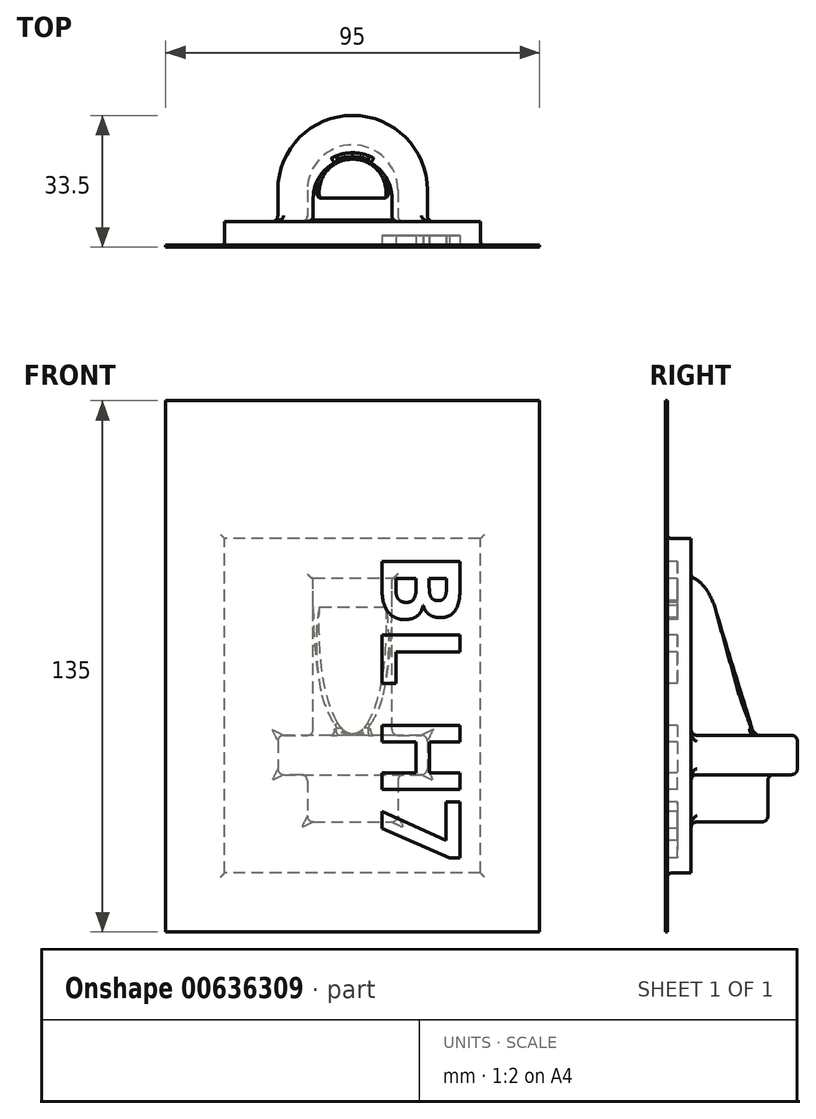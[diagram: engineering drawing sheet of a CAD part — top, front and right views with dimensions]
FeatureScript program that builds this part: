
annotation { "Feature Type Name" : "Feature", "Feature Type Description" : "" }
export const myFeature = defineFeature(function(context is Context, id is Id, definition is map)
    precondition{}
    {
        {
            var Q0;
            Q0=qCreatedBy(makeId("Right.planeOp"),FACE);
            var sketch = newSketch(context, id + "F0", { "sketchPlane" : qUnion([Q0])});
            skLineSegment(sketch, "E0", {"start": v(0, 0) * mm, "end": v(0, 135) * mm});
            skLineSegment(sketch, "E1", {"start": v(0, 135) * mm, "end": v(0.5, 135) * mm});
            skLineSegment(sketch, "E2", {"start": v(0.5, 135) * mm, "end": v(0.5, 100) * mm});
            skLineSegment(sketch, "E3", {"start": v(0.5, 100) * mm, "end": v(35.5, 100) * mm});
            skLineSegment(sketch, "E4", {"start": v(35.5, 100) * mm, "end": v(35.5, 15) * mm});
            skLineSegment(sketch, "E5", {"start": v(35.5, 15) * mm, "end": v(0.5, 15) * mm});
            skLineSegment(sketch, "E6", {"start": v(0.5, 15) * mm, "end": v(0.5, 0) * mm});
            skLineSegment(sketch, "E7", {"start": v(0.5, 0) * mm, "end": v(0, 0) * mm});
            skSolve(sketch);
        }
        {
            var Q0;
            Q0=qSketchRegion(id+"F0",true);
            extrude(context, id + "F1", {"entities" : qUnion([Q0]), "depth" : 95 * mm, "offsetDistance" : 25 * mm});
        }
        {
            var Q0;
            Q0=makeQuery(id+"F1.opExtrude","SWEPT_FACE",FACE,{"disambiguationData":[OSD([sQuery(id+"F0.wireOp",EDGE,"E4")])]});
            var sketch = newSketch(context, id + "F2", { "sketchPlane" : qUnion([Q0])});
            skLineSegment(sketch, "E8.bottom", {"start": v(-95, 100) * mm, "end": v(-80, 100) * mm});
            skLineSegment(sketch, "E8.top", {"start": v(-95, 15) * mm, "end": v(-80, 15) * mm});
            skLineSegment(sketch, "E8.left", {"start": v(-95, 100) * mm, "end": v(-95, 15) * mm});
            skLineSegment(sketch, "E8.right", {"start": v(-80, 100) * mm, "end": v(-80, 15) * mm});
            skLineSegment(sketch, "E9.bottom", {"start": v(0, 100) * mm, "end": v(-15, 100) * mm});
            skLineSegment(sketch, "E9.top", {"start": v(0, 15) * mm, "end": v(-15, 15) * mm});
            skLineSegment(sketch, "E9.left", {"start": v(0, 100) * mm, "end": v(0, 15) * mm});
            skLineSegment(sketch, "E9.right", {"start": v(-15, 100) * mm, "end": v(-15, 15) * mm});
            skSolve(sketch);
        }
        {
            var Q0;
            Q0=qSketchRegion(id+"F2",true);
            var Q1;
            Q1=makeQuery(id+"F1.opExtrude","SWEPT_FACE",FACE,{"disambiguationData":[OSD([sQuery(id+"F0.wireOp",EDGE,"E2")])]});
            extrude(context, id + "F3", {"entities" : qUnion([Q0]), "operationType" : NewBodyOperationType.REMOVE, "endBound" : BoundingType.UP_TO_SURFACE, "oppositeDirection" : true, "depth" : 25 * mm, "endBoundEntityFace" : qUnion([Q1]), "offsetDistance" : 25 * mm});
        }
        {
            var Q0;
            Q0=makeQuery(id+"F1.opExtrude","SWEPT_FACE",FACE,{"disambiguationData":[OSD([sQuery(id+"F0.wireOp",EDGE,"E0")])]});
            var sketch = newSketch(context, id + "F4", { "sketchPlane" : qUnion([Q0])});
            skText(sketch, "E10", { "text": "BL H7", "fontName": "OpenSans-Bold.ttf"});
            const initialGuessF4  = {"E10": [0.055, 0.0966, 0, -1, 0.02]};
            skSetInitialGuess(sketch, initialGuessF4);
            skSolve(sketch);
        }
        {
            var Q0;
            Q0 = qSketchRegion(id + "F4", true);
            extrude(context, id + "F5", {"entities" : qUnion([Q0]), "operationType" : NewBodyOperationType.REMOVE, "oppositeDirection" : true, "depth" : 3 * mm, "offsetDistance" : 25 * mm});
        }
        {
            var Q0;
            Q0=makeQuery(id+"F1.opExtrude","SWEPT_FACE",FACE,{"disambiguationData":[OSD([sQuery(id+"F0.wireOp",EDGE,"E5")])]});
            var sketch = newSketch(context, id + "F6", { "sketchPlane" : qUnion([Q0])});
            skLineSegment(sketch, "E11", {"start": v(80, -6.5) * mm, "end": v(66.5, -6.5) * mm});
            skLineSegment(sketch, "E12", {"start": v(47.5, -3.09) * mm, "end": v(47.5, -30.76) * mm, "construction": true});
            skPoint(sketch, "E12.startSnap0", {"position": v(47.5, -6.5) * mm});
            skLineSegment(sketch, "E13", {"start": v(66.5, -6.5) * mm, "end": v(66.5, -14.5) * mm});
            skLineSegment(sketch, "E14", {"start": v(28.5, -6.5) * mm, "end": v(28.5, -14.5) * mm});
            skArc(sketch, "E15", {"start": v(66.5, -14.5) * mm, "mid": v(47.5, -33.5) * mm, "end": v(28.5, -14.5) * mm});
            skLineSegment(sketch, "E16", {"start": v(80, -6.5) * mm, "end": v(83.42, -6.5) * mm});
            skLineSegment(sketch, "E17", {"start": v(83.42, -6.5) * mm, "end": v(83.42, -40.14) * mm});
            skLineSegment(sketch, "E18", {"start": v(83.42, -40.14) * mm, "end": v(10.55, -40.14) * mm});
            skLineSegment(sketch, "E19", {"start": v(10.55, -40.14) * mm, "end": v(10.55, -6.5) * mm});
            skLineSegment(sketch, "E20", {"start": v(10.55, -6.5) * mm, "end": v(15, -6.5) * mm});
            skLineSegment(sketch, "E21.trimOffspring", {"start": v(28.5, -6.5) * mm, "end": v(15, -6.5) * mm});
            skLineSegment(sketch, "E22.0", {"start": v(36, -6.5) * mm, "end": v(36, -14.5) * mm});
            skArc(sketch, "E22.1", {"start": v(59, -14.5) * mm, "mid": v(47.5, -26) * mm, "end": v(36, -14.5) * mm});
            skLineSegment(sketch, "E22.2", {"start": v(59, -6.5) * mm, "end": v(59, -14.5) * mm});
            skLineSegment(sketch, "E23", {"start": v(66.5, -6.5) * mm, "end": v(59, -6.5) * mm});
            skLineSegment(sketch, "E24", {"start": v(36, -6.5) * mm, "end": v(28.5, -6.5) * mm});
            skSolve(sketch);
        }
        {
            var Q0;
            {var subQ4=sQuery(id+"F6.wireOp",EDGE,"E16");Q0=makeQuery(id+"F6.imprint","IMPRINT",FACE,{"disambiguationData":[TD([[makeQuery(id+"F6.imprint","IMPRINT",EDGE,{"derivedFrom":subQ4}),-1.0]])]});}
            var Q1;
            {var subQ0=sQuery(id+"F6.wireOp",EDGE,"E11");Q1=makeQuery(id+"F6.imprint","IMPRINT",FACE,{"disambiguationData":[TD([[makeQuery(id+"F6.imprint","IMPRINT",EDGE,{"derivedFrom":subQ0}),1.0]])]});}
            var Q2;
            Q2=makeQuery(id+"F1.opExtrude","SWEPT_FACE",FACE,{"disambiguationData":[OSD([sQuery(id+"F0.wireOp",EDGE,"E3")])]});
            extrude(context, id + "F7", {"entities" : qUnion([Q0, Q1]), "operationType" : NewBodyOperationType.REMOVE, "endBound" : BoundingType.UP_TO_SURFACE, "oppositeDirection" : true, "depth" : 20 * mm, "endBoundEntityFace" : qUnion([Q2]), "offsetDistance" : 25 * mm});
        }
        {
            var Q0;
            Q0 = qSketchRegion(id + "F6", true);
            extrude(context, id + "F8", {"entities" : qUnion([Q0]), "operationType" : NewBodyOperationType.REMOVE, "oppositeDirection" : true, "depth" : 25 * mm, "offsetDistance" : 25 * mm});
        }
        {
            var Q0;
            Q0=makeQuery(id+"F1.opExtrude","SWEPT_FACE",FACE,{"disambiguationData":[OSD([sQuery(id+"F0.wireOp",EDGE,"E3")])]});
            var sketch = newSketch(context, id + "F9", { "sketchPlane" : qUnion([Q0])});
            skLineSegment(sketch, "E25", {"start": v(28.5, 6.5) * mm, "end": v(37.5, 6.5) * mm});
            skPoint(sketch, "E26", {"position": v(47.5, 6.5) * mm});
            skLineSegment(sketch, "E27", {"start": v(37.5, 6.5) * mm, "end": v(37.5, 12.5) * mm});
            skLineSegment(sketch, "E28", {"start": v(57.5, 6.5) * mm, "end": v(57.5, 12.5) * mm});
            skLineSegment(sketch, "E29", {"start": v(47.5, 3.35) * mm, "end": v(47.5, 29.33) * mm, "construction": true});
            skArc(sketch, "E30", {"start": v(37.5, 12.5) * mm, "mid": v(47.5, 22.5) * mm, "end": v(57.5, 12.5) * mm});
            skLineSegment(sketch, "E31", {"start": v(28.5, 6.5) * mm, "end": v(24.68, 6.5) * mm});
            skLineSegment(sketch, "E32", {"start": v(24.68, 6.5) * mm, "end": v(24.68, 41.76) * mm});
            skLineSegment(sketch, "E33", {"start": v(24.68, 41.76) * mm, "end": v(72, 41.76) * mm});
            skLineSegment(sketch, "E34", {"start": v(72, 41.76) * mm, "end": v(72, 6.5) * mm});
            skLineSegment(sketch, "E35", {"start": v(72, 6.5) * mm, "end": v(66.5, 6.5) * mm});
            skLineSegment(sketch, "E36.trimOffspring", {"start": v(57.5, 6.5) * mm, "end": v(66.5, 6.5) * mm});
            skSolve(sketch);
        }
        {
            var Q0;
            Q0 = qSketchRegion(id + "F9", true);
            extrude(context, id + "F10", {"entities" : qUnion([Q0]), "operationType" : NewBodyOperationType.REMOVE, "oppositeDirection" : true, "depth" : 50 * mm, "offsetDistance" : 25 * mm});
        }
        {
            var Q0;
            Q0=makeQuery(id+"F3.boolean.opBoolean","COPY",FACE,{"derivedFrom":makeQuery(id+"F3.opExtrude","SWEPT_FACE",FACE,{"disambiguationData":[OSD([sQuery(id+"F2.wireOp",EDGE,"E8.right")])]})});
            var sketch = newSketch(context, id + "F11", { "sketchPlane" : qUnion([Q0])});
            skLineSegment(sketch, "E37", {"start": v(6.5, 106.69) * mm, "end": v(6.5, 100) * mm});
            skLineSegment(sketch, "E38", {"start": v(6.5, 100) * mm, "end": v(6.5, 90) * mm});
            skLineSegment(sketch, "E39", {"start": v(6.5, 90) * mm, "end": v(30.58, 90) * mm});
            skLineSegment(sketch, "E40", {"start": v(30.58, 90) * mm, "end": v(30.58, 106.69) * mm});
            skLineSegment(sketch, "E41", {"start": v(30.58, 106.69) * mm, "end": v(6.5, 106.69) * mm});
            skLineSegment(sketch, "E42", {"start": v(6.5, 15) * mm, "end": v(6.5, 28) * mm});
            skLineSegment(sketch, "E43", {"start": v(6.5, 28) * mm, "end": v(39.5, 28) * mm});
            skLineSegment(sketch, "E44", {"start": v(39.5, 28) * mm, "end": v(39.5, 8.96) * mm});
            skLineSegment(sketch, "E45", {"start": v(39.5, 8.96) * mm, "end": v(6.5, 8.96) * mm});
            skLineSegment(sketch, "E46", {"start": v(6.5, 8.96) * mm, "end": v(6.5, 15) * mm});
            skSolve(sketch);
        }
        {
            var Q0;
            Q0 = qSketchRegion(id + "F11", true);
            var Q1;
            Q1=makeQuery(id+"F3.boolean.opBoolean","COPY",FACE,{"derivedFrom":makeQuery(id+"F3.opExtrude","SWEPT_FACE",FACE,{"disambiguationData":[OSD([sQuery(id+"F2.wireOp",EDGE,"E9.right")])]})});
            extrude(context, id + "F12", {"entities" : qUnion([Q0]), "operationType" : NewBodyOperationType.REMOVE, "endBound" : BoundingType.UP_TO_SURFACE, "oppositeDirection" : true, "depth" : 25 * mm, "endBoundEntityFace" : qUnion([Q1]), "offsetDistance" : 25 * mm});
        }
        {
            var Q0;
            Q0=makeQuery(id+"F10.boolean.opBoolean","COPY",FACE,{"derivedFrom":makeQuery(id+"F10.opExtrude","SWEPT_FACE",FACE,{"disambiguationData":[OSD([sQuery(id+"F9.wireOp",EDGE,"E28")])]})});
            var sketch = newSketch(context, id + "F13", { "sketchPlane" : qUnion([Q0])});
            skLineSegment(sketch, "E47.0", {"start": v(6.5, 90) * mm, "end": v(12.5, 90) * mm});
            skLineSegment(sketch, "E48", {"start": v(22.5, 50) * mm, "end": v(12.5, 82.56) * mm});
            skFitSpline(sketch, "E49", {"points": [v(12.5, 82.56) * mm, v(6.5, 90) * mm, v(4.86, 86.58) * mm], "startDerivative": vector(-6, 21.53) * mm, "endDerivative": vector(-3.18, -12.9) * mm});
            skLineSegment(sketch, "E50", {"start": v(6.5, 90) * mm, "end": v(6.5, 93.08) * mm});
            skLineSegment(sketch, "E51", {"start": v(6.5, 93.08) * mm, "end": v(28.2, 93.08) * mm});
            skLineSegment(sketch, "E52", {"start": v(22.5, 50) * mm, "end": v(28.2, 93.08) * mm});
            skSolve(sketch);
        }
        {
            var Q0;
            Q0 = qSketchRegion(id + "F13", true);
            extrude(context, id + "F14", {"entities" : qUnion([Q0]), "operationType" : NewBodyOperationType.REMOVE, "oppositeDirection" : true, "depth" : 25 * mm, "offsetDistance" : 25 * mm});
        }
        {
            var Q0;
            Q0=makeQuery(id+"F10.boolean.opBoolean","COPY",EDGE,{"derivedFrom":makeQuery(id+"F10.opExtrude","SWEPT_EDGE",EDGE,{"disambiguationData":[OSD([sQuery(id+"F9.wireOp",EDGE,"E28"),sQuery(id+"F9.wireOp",EDGE,"E36.trimOffspring")])]})});
            var Q1;
            Q1=makeQuery(id+"F12.boolean.opBoolean","COPY",EDGE,{"derivedFrom":makeQuery(id+"F12.opExtrude","SWEPT_EDGE",EDGE,{"disambiguationData":[OSD([sQuery(id+"F2.wireOp",EDGE,"E8.right"),sQuery(id+"F6.wireOp",EDGE,"E11"),sQuery(id+"F6.wireOp",EDGE,"E16"),sQuery(id+"F11.wireOp",EDGE,"E38"),sQuery(id+"F11.wireOp",EDGE,"E39")])]})});
            var Q2;
            Q2=makeQuery(id+"F10.boolean.opBoolean","COPY",EDGE,{"derivedFrom":makeQuery(id+"F10.opExtrude","CAP_EDGE",EDGE,{"disambiguationData":[OSD([sQuery(id+"F9.wireOp",EDGE,"E35"),sQuery(id+"F9.wireOp",EDGE,"E36.trimOffspring")])],"isStart":false})});
            var Q3;
            Q3=makeQuery(id+"F7.boolean.opBoolean","COPY",EDGE,{"derivedFrom":makeQuery(id+"F7.opExtrude","SWEPT_EDGE",EDGE,{"disambiguationData":[OSD([sQuery(id+"F6.wireOp",EDGE,"E11"),sQuery(id+"F6.wireOp",EDGE,"E13"),sQuery(id+"F6.wireOp",EDGE,"E23")])]})});
            var Q4;
            Q4=makeQuery(id+"F8.boolean.opBoolean","COPY",EDGE,{"derivedFrom":makeQuery(id+"F8.opExtrude","CAP_EDGE",EDGE,{"disambiguationData":[OSD([sQuery(id+"F6.wireOp",EDGE,"E11"),sQuery(id+"F6.wireOp",EDGE,"E16"),sQuery(id+"F6.wireOp",EDGE,"E23")])],"isStart":false})});
            var Q5;
            Q5=makeQuery(id+"F8.boolean.opBoolean","COPY",EDGE,{"derivedFrom":makeQuery(id+"F8.opExtrude","SWEPT_EDGE",EDGE,{"disambiguationData":[OSD([sQuery(id+"F6.wireOp",EDGE,"E22.2"),sQuery(id+"F6.wireOp",EDGE,"E23")])]})});
            var Q6;
            Q6=makeQuery(id+"F12.boolean.opBoolean","COPY",EDGE,{"derivedFrom":makeQuery(id+"F12.opExtrude","SWEPT_EDGE",EDGE,{"disambiguationData":[OSD([sQuery(id+"F2.wireOp",EDGE,"E8.right"),sQuery(id+"F6.wireOp",EDGE,"E11"),sQuery(id+"F6.wireOp",EDGE,"E16"),sQuery(id+"F11.wireOp",EDGE,"E42"),sQuery(id+"F11.wireOp",EDGE,"E43")])]})});
            var Q7;
            Q7=makeQuery(id+"F8.boolean.opBoolean","COPY",EDGE,{"derivedFrom":makeQuery(id+"F8.opExtrude","SWEPT_EDGE",EDGE,{"disambiguationData":[OSD([sQuery(id+"F6.wireOp",EDGE,"E22.0"),sQuery(id+"F6.wireOp",EDGE,"E24")])]})});
            var Q8;
            Q8=makeQuery(id+"F8.boolean.opBoolean","COPY",EDGE,{"derivedFrom":makeQuery(id+"F8.opExtrude","CAP_EDGE",EDGE,{"disambiguationData":[OSD([sQuery(id+"F6.wireOp",EDGE,"E20"),sQuery(id+"F6.wireOp",EDGE,"E21.trimOffspring"),sQuery(id+"F6.wireOp",EDGE,"E24")])],"isStart":false})});
            var Q9;
            Q9=makeQuery(id+"F7.boolean.opBoolean","COPY",EDGE,{"derivedFrom":makeQuery(id+"F7.opExtrude","SWEPT_EDGE",EDGE,{"disambiguationData":[OSD([sQuery(id+"F6.wireOp",EDGE,"E14"),sQuery(id+"F6.wireOp",EDGE,"E21.trimOffspring"),sQuery(id+"F6.wireOp",EDGE,"E24")])]})});
            var Q10;
            Q10=makeQuery(id+"F10.boolean.opBoolean","COPY",EDGE,{"derivedFrom":makeQuery(id+"F10.opExtrude","CAP_EDGE",EDGE,{"disambiguationData":[OSD([sQuery(id+"F9.wireOp",EDGE,"E25"),sQuery(id+"F9.wireOp",EDGE,"E31")])],"isStart":false})});
            var Q11;
            Q11=makeQuery(id+"F10.boolean.opBoolean","COPY",EDGE,{"derivedFrom":makeQuery(id+"F10.opExtrude","SWEPT_EDGE",EDGE,{"disambiguationData":[OSD([sQuery(id+"F9.wireOp",EDGE,"E25"),sQuery(id+"F9.wireOp",EDGE,"E27")])]})});
            fillet(context, id + "F15", {"entities" : qUnion([Q0, Q1, Q2, Q3, Q4, Q5, Q6, Q7, Q8, Q9, Q10, Q11]), "radius" : 1.5 * mm, "tangentPropagation" : true, "allowEdgeOverflow" : false});
        }
        {
            var Q0;
            {var subQ0=sQuery(id+"F9.wireOp",EDGE,"E30");var subQ1=sQuery(id+"F9.wireOp",EDGE,"E28");Q0=makeQuery(id+"F14.boolean.opBoolean","SPLIT",EDGE,{"disambiguationData":[TD([makeQuery(id+"F10.boolean.opBoolean","COPY",FACE,{"derivedFrom":makeQuery(id+"F10.opExtrude","SWEPT_FACE",FACE,{"disambiguationData":[OSD([subQ1])]})})])],"derivedFrom":makeQuery(id+"F10.boolean.opBoolean","COPY",EDGE,{"derivedFrom":makeQuery(id+"F10.opExtrude","CAP_EDGE",EDGE,{"disambiguationData":[OSD([subQ0])],"isStart":false})})});}
            var Q1;
            Q1=makeQuery(id+"F14.boolean.opBoolean","INTERSECT",EDGE,{"disambiguationData":[OD(1.0)],"derivedFrom":[makeQuery(id+"F10.boolean.opBoolean","COPY",FACE,{"derivedFrom":makeQuery(id+"F10.opExtrude","SWEPT_FACE",FACE,{"disambiguationData":[OSD([sQuery(id+"F9.wireOp",EDGE,"E30")])]})}),makeQuery(id+"F14.opExtrude","SWEPT_FACE",FACE,{"disambiguationData":[OSD([sQuery(id+"F13.wireOp",EDGE,"E48")])]})]});
            var Q2;
            Q2=makeQuery(id+"F14.boolean.opBoolean","INTERSECT",EDGE,{"disambiguationData":[OD(0.0)],"derivedFrom":[makeQuery(id+"F10.boolean.opBoolean","COPY",FACE,{"derivedFrom":makeQuery(id+"F10.opExtrude","SWEPT_FACE",FACE,{"disambiguationData":[OSD([sQuery(id+"F9.wireOp",EDGE,"E30")])]})}),makeQuery(id+"F14.opExtrude","SWEPT_FACE",FACE,{"disambiguationData":[OSD([sQuery(id+"F13.wireOp",EDGE,"E48")])]})]});
            var Q3;
            {var subQ0=sQuery(id+"F9.wireOp",EDGE,"E30");var subQ1=sQuery(id+"F9.wireOp",EDGE,"E27");Q3=makeQuery(id+"F14.boolean.opBoolean","SPLIT",EDGE,{"disambiguationData":[TD([makeQuery(id+"F10.boolean.opBoolean","COPY",FACE,{"derivedFrom":makeQuery(id+"F10.opExtrude","SWEPT_FACE",FACE,{"disambiguationData":[OSD([subQ1])]})})])],"derivedFrom":makeQuery(id+"F10.boolean.opBoolean","COPY",EDGE,{"derivedFrom":makeQuery(id+"F10.opExtrude","CAP_EDGE",EDGE,{"disambiguationData":[OSD([subQ0])],"isStart":false})})});}
            fillet(context, id + "F16", {"entities" : qUnion([Q0, Q1, Q2, Q3]), "radius" : 1.5 * mm, "tangentPropagation" : true, "allowEdgeOverflow" : false});
        }
        {
            var Q0;
            Q0=makeQuery(id+"F1.opExtrude","SWEPT_EDGE",EDGE,{"disambiguationData":[OSD([sQuery(id+"F0.wireOp",EDGE,"E2"),sQuery(id+"F0.wireOp",EDGE,"E3")])]});
            var Q1;
            Q1=makeQuery(id+"F3.boolean.opBoolean","COPY",EDGE,{"derivedFrom":makeQuery(id+"F3.opExtrude","CAP_EDGE",EDGE,{"disambiguationData":[OSD([sQuery(id+"F2.wireOp",EDGE,"E8.right")])],"isStart":false})});
            var Q2;
            Q2=makeQuery(id+"F3.boolean.opBoolean","COPY",EDGE,{"derivedFrom":makeQuery(id+"F3.opExtrude","CAP_EDGE",EDGE,{"disambiguationData":[OSD([sQuery(id+"F2.wireOp",EDGE,"E9.right")])],"isStart":false})});
            var Q3;
            Q3=makeQuery(id+"F1.opExtrude","SWEPT_EDGE",EDGE,{"disambiguationData":[OSD([sQuery(id+"F0.wireOp",EDGE,"E5"),sQuery(id+"F0.wireOp",EDGE,"E6")])]});
            fillet(context, id + "F17", {"entities" : qUnion([Q0, Q1, Q2, Q3]), "radius" : 1 * mm, "tangentPropagation" : true, "allowEdgeOverflow" : false});
        }
        {
            var Q0;
            Q0=makeQuery(id+"F10.boolean.opBoolean","COPY",FACE,{"derivedFrom":makeQuery(id+"F10.opExtrude","CAP_FACE",FACE,{"disambiguationData":[OSD([sQuery(id+"F9.wireOp",EDGE,"E25"),sQuery(id+"F9.wireOp",EDGE,"E27"),sQuery(id+"F9.wireOp",EDGE,"E28"),sQuery(id+"F9.wireOp",EDGE,"E30"),sQuery(id+"F9.wireOp",EDGE,"E31"),sQuery(id+"F9.wireOp",EDGE,"E32"),sQuery(id+"F9.wireOp",EDGE,"E33"),sQuery(id+"F9.wireOp",EDGE,"E34"),sQuery(id+"F9.wireOp",EDGE,"E35"),sQuery(id+"F9.wireOp",EDGE,"E36.trimOffspring")])],"isStart":false})});
            var Q1;
            Q1=makeQuery(id+"F8.boolean.opBoolean","COPY",FACE,{"derivedFrom":makeQuery(id+"F8.opExtrude","CAP_FACE",FACE,{"disambiguationData":[OSD([sQuery(id+"F6.wireOp",EDGE,"E11"),sQuery(id+"F6.wireOp",EDGE,"E16"),sQuery(id+"F6.wireOp",EDGE,"E17"),sQuery(id+"F6.wireOp",EDGE,"E18"),sQuery(id+"F6.wireOp",EDGE,"E19"),sQuery(id+"F6.wireOp",EDGE,"E20"),sQuery(id+"F6.wireOp",EDGE,"E21.trimOffspring"),sQuery(id+"F6.wireOp",EDGE,"E22.0"),sQuery(id+"F6.wireOp",EDGE,"E22.1"),sQuery(id+"F6.wireOp",EDGE,"E22.2"),sQuery(id+"F6.wireOp",EDGE,"E23"),sQuery(id+"F6.wireOp",EDGE,"E24")])],"isStart":false})});
            var Q2;
            Q2=makeQuery(id+"F12.boolean.opBoolean","COPY",FACE,{"derivedFrom":makeQuery(id+"F12.opExtrude","SWEPT_FACE",FACE,{"disambiguationData":[OSD([sQuery(id+"F11.wireOp",EDGE,"E43")])]})});
            fillet(context, id + "F18", {"entities" : qUnion([Q0, Q1, Q2]), "radius" : 1.5 * mm, "tangentPropagation" : true, "allowEdgeOverflow" : false});
        }
    });
